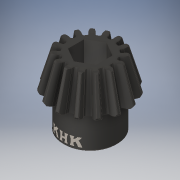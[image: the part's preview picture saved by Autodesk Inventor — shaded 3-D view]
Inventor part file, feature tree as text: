
AUTODESK INVENTOR PART (.ipt)
format: ipt  version: 2019.3 (Build 233278000, 278)  size: 1,502,208 bytes
history: native  units: in
note: dims shown in document units (in); Inventor stores cm internally (conversion verified against a paired STEP export)
features: extrude x1, sketch x1, imported_body x1
ambient origin geometry x8: Origin, YZ Plane, XZ Plane, XY Plane, X Axis, Y Axis, Z Axis, Center Point
bodies: Solid1 (feature_tree)
feature tree (3):
  extrude  "Extrusion1"  Depth=0.375in TaperAngle=0.0deg
  sketch  "Sketch1"  dims[d0=0.375in d1=0.3937in d2=0.0in]
  imported_body  "Base1"
